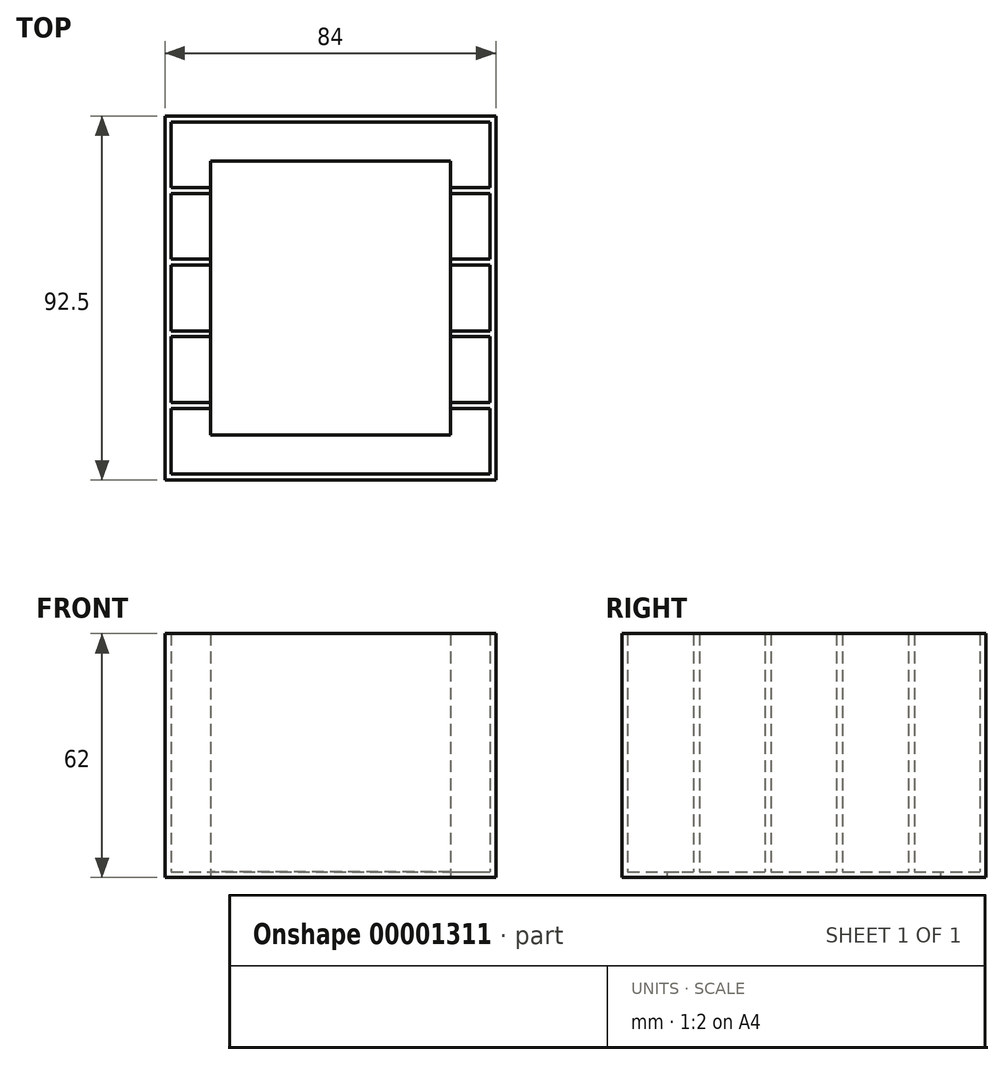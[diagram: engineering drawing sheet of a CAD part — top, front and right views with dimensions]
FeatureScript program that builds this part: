
annotation { "Feature Type Name" : "Feature", "Feature Type Description" : "" }
export const myFeature = defineFeature(function(context is Context, id is Id, definition is map)
    precondition{}
    {
        {
            var Q0;
            Q0=qCreatedBy(makeId("Top.planeOp"),FACE);
            var sketch = newSketch(context, id + "F0", { "sketchPlane" : qUnion([Q0])});
            skLineSegment(sketch, "E0.bottom", {"start": v(0, 0) * mm, "end": v(84, 0) * mm});
            skLineSegment(sketch, "E0.top", {"start": v(0, 92.5) * mm, "end": v(84, 92.5) * mm});
            skLineSegment(sketch, "E0.left", {"start": v(0, 0) * mm, "end": v(0, 92.5) * mm});
            skLineSegment(sketch, "E0.right", {"start": v(84, 0) * mm, "end": v(84, 92.5) * mm});
            skSolve(sketch);
        }
        {
            var Q0;
            Q0=makeQuery(id+"F0.imprint","IMPRINT",FACE,{"disambiguationData":[TD([[makeQuery(id+"F0.imprint","IMPRINT",EDGE,{"derivedFrom":sQuery(id+"F0.wireOp",EDGE,"E0.bottom")}),1.0]])]});
            extrude(context, id + "F1", {"entities" : qUnion([Q0]), "depth" : 62 * mm});
        }
        {
            var Q0;
            Q0=makeQuery(id+"F1.opExtrude","CAP_FACE",FACE,{"disambiguationData":[OSD([sQuery(id+"F0.wireOp",EDGE,"E0.bottom"),sQuery(id+"F0.wireOp",EDGE,"E0.top"),sQuery(id+"F0.wireOp",EDGE,"E0.left"),sQuery(id+"F0.wireOp",EDGE,"E0.right")])],"isStart":false});
            shell(context, id + "F2", {"entities" : qUnion([Q0]), "thickness" : 1.5 * mm});
        }
        {
            var Q0;
            Q0=makeQuery(id+"F2.opShell","OFFSET_FACE",FACE,{"disambiguationData":[OSD([sQuery(id+"F0.wireOp",EDGE,"E0.bottom"),sQuery(id+"F0.wireOp",EDGE,"E0.top"),sQuery(id+"F0.wireOp",EDGE,"E0.left"),sQuery(id+"F0.wireOp",EDGE,"E0.right")])]});
            var sketch = newSketch(context, id + "F3", { "sketchPlane" : qUnion([Q0])});
            skLineSegment(sketch, "E1.bottom", {"start": v(1.5, 19.7) * mm, "end": v(82.5, 19.7) * mm});
            skLineSegment(sketch, "E1.top", {"start": v(1.5, 18.2) * mm, "end": v(82.5, 18.2) * mm});
            skLineSegment(sketch, "E1.left", {"start": v(1.5, 19.7) * mm, "end": v(1.5, 18.2) * mm});
            skLineSegment(sketch, "E1.right", {"start": v(82.5, 19.7) * mm, "end": v(82.5, 18.2) * mm});
            skLineSegment(sketch, "E2.bottom", {"start": v(1.5, 37.9) * mm, "end": v(82.5, 37.9) * mm});
            skLineSegment(sketch, "E2.top", {"start": v(1.5, 36.4) * mm, "end": v(82.5, 36.4) * mm});
            skLineSegment(sketch, "E2.left", {"start": v(1.5, 37.9) * mm, "end": v(1.5, 36.4) * mm});
            skLineSegment(sketch, "E2.right", {"start": v(82.5, 37.9) * mm, "end": v(82.5, 36.4) * mm});
            skLineSegment(sketch, "E3.bottom", {"start": v(1.5, 74.3) * mm, "end": v(82.5, 74.3) * mm});
            skLineSegment(sketch, "E3.top", {"start": v(1.5, 72.8) * mm, "end": v(82.5, 72.8) * mm});
            skLineSegment(sketch, "E3.left", {"start": v(1.5, 74.3) * mm, "end": v(1.5, 72.8) * mm});
            skLineSegment(sketch, "E3.right", {"start": v(82.5, 74.3) * mm, "end": v(82.5, 72.8) * mm});
            skLineSegment(sketch, "E4.bottom", {"start": v(1.5, 56.1) * mm, "end": v(82.5, 56.1) * mm});
            skLineSegment(sketch, "E4.top", {"start": v(1.5, 54.6) * mm, "end": v(82.5, 54.6) * mm});
            skLineSegment(sketch, "E4.left", {"start": v(1.5, 56.1) * mm, "end": v(1.5, 54.6) * mm});
            skLineSegment(sketch, "E4.right", {"start": v(82.5, 56.1) * mm, "end": v(82.5, 54.6) * mm});
            skSolve(sketch);
        }
        {
            var Q0;
            Q0=makeQuery(id+"F3.imprint","IMPRINT",FACE,{"disambiguationData":[TD([[makeQuery(id+"F3.imprint","IMPRINT",EDGE,{"derivedFrom":sQuery(id+"F3.wireOp",EDGE,"E1.bottom")}),-1.0]])]});
            var Q1;
            Q1=makeQuery(id+"F3.imprint","IMPRINT",FACE,{"disambiguationData":[TD([[makeQuery(id+"F3.imprint","IMPRINT",EDGE,{"derivedFrom":sQuery(id+"F3.wireOp",EDGE,"E2.bottom")}),-1.0]])]});
            var Q2;
            Q2=makeQuery(id+"F3.imprint","IMPRINT",FACE,{"disambiguationData":[TD([[makeQuery(id+"F3.imprint","IMPRINT",EDGE,{"derivedFrom":sQuery(id+"F3.wireOp",EDGE,"E4.bottom")}),-1.0]])]});
            var Q3;
            Q3=makeQuery(id+"F3.imprint","IMPRINT",FACE,{"disambiguationData":[TD([[makeQuery(id+"F3.imprint","IMPRINT",EDGE,{"derivedFrom":sQuery(id+"F3.wireOp",EDGE,"E3.bottom")}),-1.0]])]});
            var Q4;
            Q4=makeQuery(id+"F1.opExtrude","CAP_FACE",FACE,{"disambiguationData":[OSD([sQuery(id+"F0.wireOp",EDGE,"E0.bottom"),sQuery(id+"F0.wireOp",EDGE,"E0.top"),sQuery(id+"F0.wireOp",EDGE,"E0.left"),sQuery(id+"F0.wireOp",EDGE,"E0.right")])],"isStart":false});
            extrude(context, id + "F4", {"entities" : qUnion([Q0, Q1, Q2, Q3]), "operationType" : NewBodyOperationType.ADD, "endBound" : BoundingType.UP_TO_SURFACE, "endBoundEntityFace" : qUnion([Q4]), "depth" : 25 * mm});
        }
        {
            var Q0;
            Q0=qCreatedBy(makeId("Top.planeOp"),FACE);
            var sketch = newSketch(context, id + "F5", { "sketchPlane" : qUnion([Q0])});
            skLineSegment(sketch, "E5.bottom", {"start": v(11.5, 81) * mm, "end": v(72.5, 81) * mm});
            skLineSegment(sketch, "E5.top", {"start": v(11.5, 11.5) * mm, "end": v(72.5, 11.5) * mm});
            skLineSegment(sketch, "E5.left", {"start": v(11.5, 81) * mm, "end": v(11.5, 11.5) * mm});
            skLineSegment(sketch, "E5.right", {"start": v(72.5, 81) * mm, "end": v(72.5, 11.5) * mm});
            skSolve(sketch);
        }
        {
            var Q0;
            Q0=makeQuery(id+"F5.imprint","IMPRINT",FACE,{"disambiguationData":[TD([[makeQuery(id+"F5.imprint","IMPRINT",EDGE,{"derivedFrom":sQuery(id+"F5.wireOp",EDGE,"E5.bottom")}),-1.0]])]});
            extrude(context, id + "F6", {"entities" : qUnion([Q0]), "operationType" : NewBodyOperationType.REMOVE, "depth" : 70 * mm});
        }
    });
